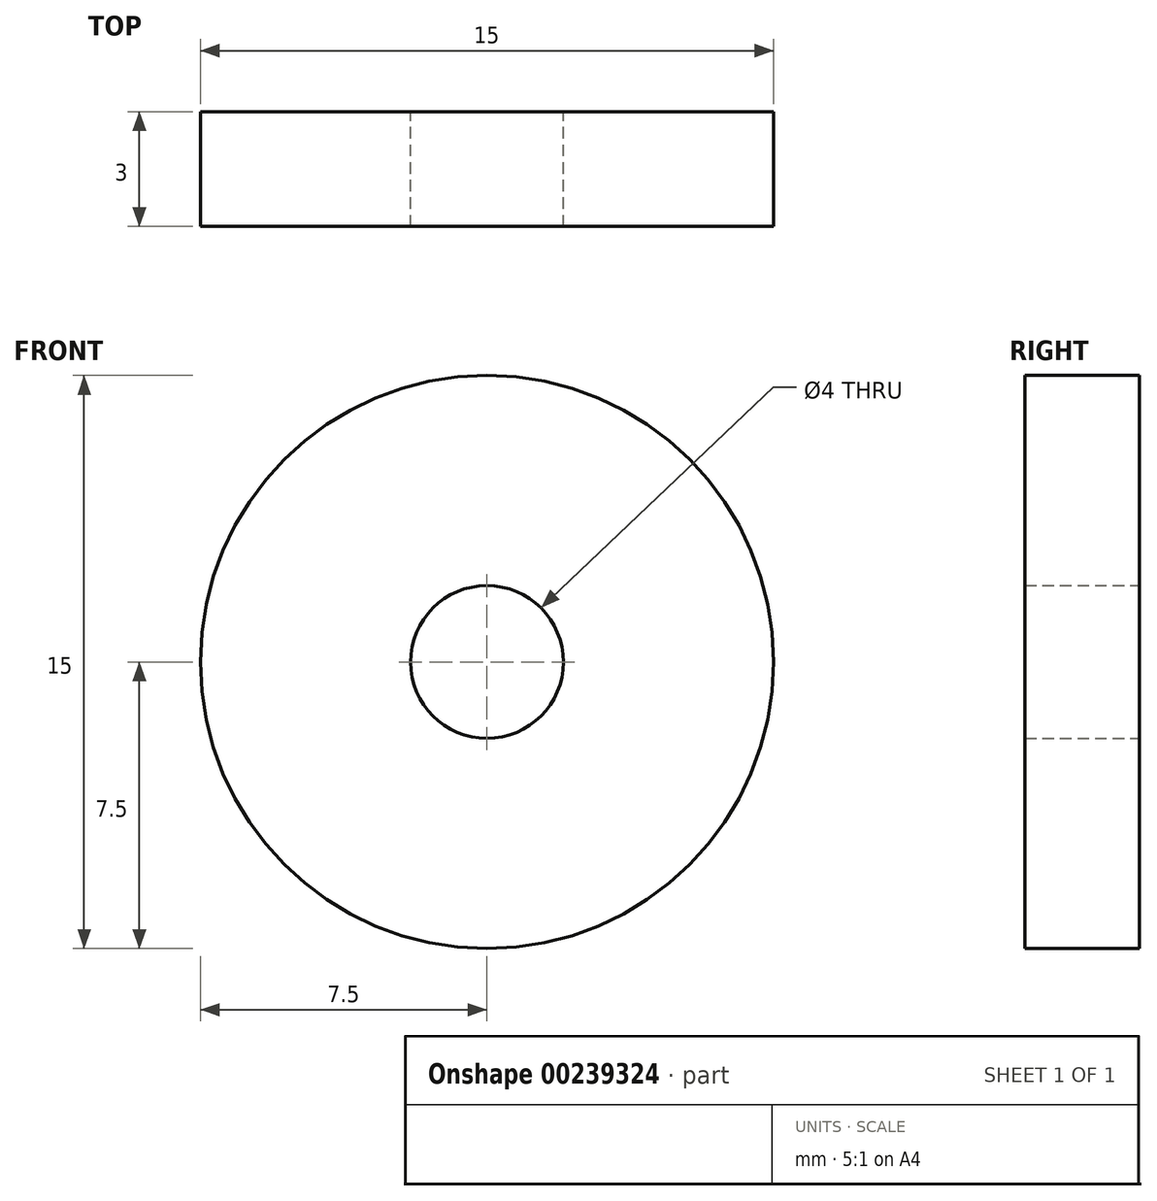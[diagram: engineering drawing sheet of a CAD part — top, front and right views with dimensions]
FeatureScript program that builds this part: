
annotation { "Feature Type Name" : "Feature", "Feature Type Description" : "" }
export const myFeature = defineFeature(function(context is Context, id is Id, definition is map)
    precondition{}
    {
        {
            var Q0;
            Q0=qCreatedBy(makeId("Front.planeOp"),FACE);
            var sketch = newSketch(context, id + "F0", { "sketchPlane" : qUnion([Q0])});
            skCircle(sketch, "E0", {"center": v(0, 0) * mm, "radius": 7.5 * mm});
            skCircle(sketch, "E1", {"center": v(0, 0) * mm, "radius": 2 * mm});
            skSolve(sketch);
        }
        {
            var Q0;
            Q0 = qSketchRegion(id + "F0", true);
            extrude(context, id + "F1", {"entities" : qUnion([Q0]), "depth" : 3 * mm});
        }
    });
